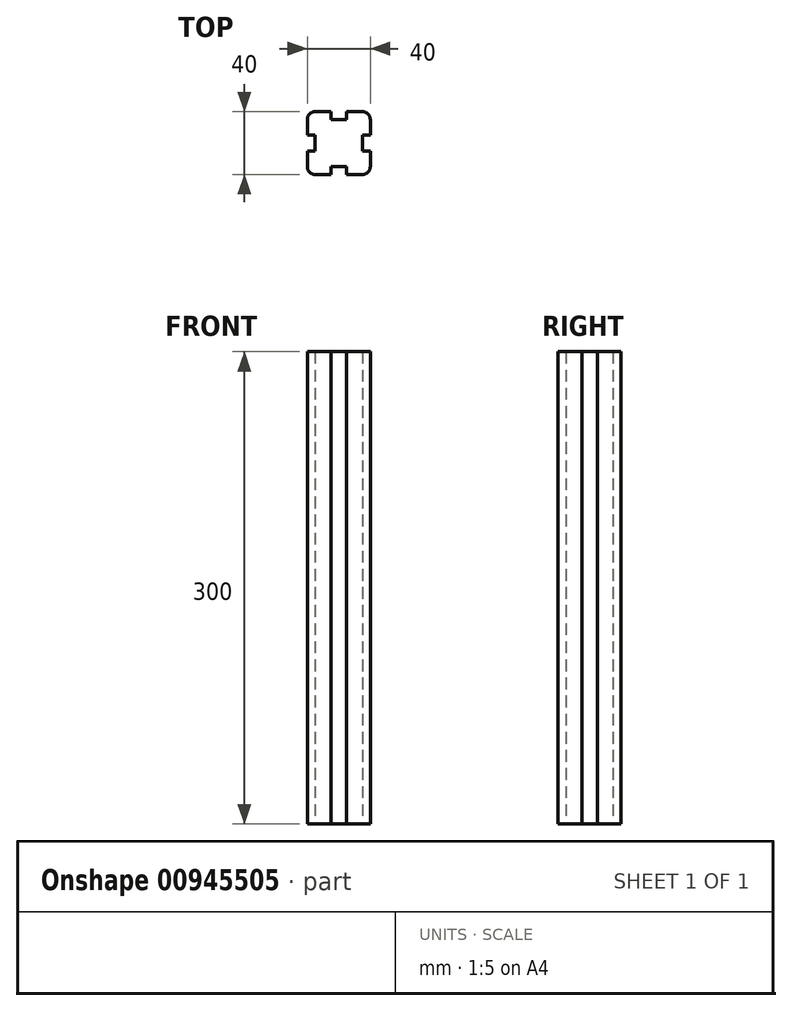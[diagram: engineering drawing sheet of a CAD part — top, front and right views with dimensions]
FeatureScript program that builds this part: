
annotation { "Feature Type Name" : "Feature", "Feature Type Description" : "" }
export const myFeature = defineFeature(function(context is Context, id is Id, definition is map)
    precondition{}
    {
        {
            var Q0;
            Q0=qCreatedBy(makeId("Top.planeOp"),FACE);
            var sketch = newSketch(context, id + "F0", { "sketchPlane" : qUnion([Q0])});
            skLineSegment(sketch, "E0.bottom", {"start": v(20, 20) * mm, "end": v(-20, 20) * mm});
            skLineSegment(sketch, "E0.top", {"start": v(20, -20) * mm, "end": v(-20, -20) * mm});
            skLineSegment(sketch, "E0.left", {"start": v(20, 20) * mm, "end": v(20, -20) * mm});
            skLineSegment(sketch, "E0.right", {"start": v(-20, 20) * mm, "end": v(-20, -20) * mm});
            skPoint(sketch, "E0.middle", {"position": v(0, 0) * mm});
            skLineSegment(sketch, "E1.bottom", {"start": v(-5, 20) * mm, "end": v(5, 20) * mm});
            skLineSegment(sketch, "E1.top", {"start": v(-5, 15) * mm, "end": v(5, 15) * mm});
            skLineSegment(sketch, "E1.left", {"start": v(-5, 20) * mm, "end": v(-5, 15) * mm});
            skLineSegment(sketch, "E1.right", {"start": v(5, 20) * mm, "end": v(5, 15) * mm});
            skLineSegment(sketch, "E2.bottom", {"start": v(-20, 5) * mm, "end": v(-15, 5) * mm});
            skLineSegment(sketch, "E2.top", {"start": v(-20, -5) * mm, "end": v(-15, -5) * mm});
            skLineSegment(sketch, "E2.left", {"start": v(-20, 5) * mm, "end": v(-20, -5) * mm});
            skLineSegment(sketch, "E2.right", {"start": v(-15, 5) * mm, "end": v(-15, -5) * mm});
            skLineSegment(sketch, "E3.MirrorCS", {"start": v(20, 5) * mm, "end": v(15, 5) * mm});
            skLineSegment(sketch, "E4.MirrorCS", {"start": v(15, 5) * mm, "end": v(15, -5) * mm});
            skLineSegment(sketch, "E5.MirrorCS", {"start": v(20, -5) * mm, "end": v(15, -5) * mm});
            skLineSegment(sketch, "E6.MirrorCS", {"start": v(-5, -20) * mm, "end": v(-5, -15) * mm});
            skLineSegment(sketch, "E7.MirrorCS", {"start": v(-5, -15) * mm, "end": v(5, -15) * mm});
            skLineSegment(sketch, "E8.MirrorCS", {"start": v(5, -20) * mm, "end": v(5, -15) * mm});
            skSolve(sketch);
        }
        {
            var Q0;
            Q0=makeQuery(id+"F0.imprint","IMPRINT",FACE,{"disambiguationData":[TD([[makeQuery(id+"F0.imprint","IMPRINT",EDGE,{"derivedFrom":sQuery(id+"F0.wireOp",EDGE,"E1.top")}),-1.0]])]});
            extrude(context, id + "F1", {"entities" : qUnion([Q0]), "endBound" : BoundingType.SYMMETRIC, "depth" : 300 * mm, "offsetDistance" : 25 * mm});
        }
        {
            var Q0;
            Q0=makeQuery(id+"F1.opExtrude","SWEPT_EDGE",EDGE,{"disambiguationData":[OSD([sQuery(id+"F0.wireOp",EDGE,"E0.bottom"),sQuery(id+"F0.wireOp",EDGE,"E0.left")])]});
            var Q1;
            Q1=makeQuery(id+"F1.opExtrude","SWEPT_EDGE",EDGE,{"disambiguationData":[OSD([sQuery(id+"F0.wireOp",EDGE,"E0.bottom"),sQuery(id+"F0.wireOp",EDGE,"E0.right")])]});
            var Q2;
            Q2=makeQuery(id+"F1.opExtrude","SWEPT_EDGE",EDGE,{"disambiguationData":[OSD([sQuery(id+"F0.wireOp",EDGE,"E0.top"),sQuery(id+"F0.wireOp",EDGE,"E0.right")])]});
            var Q3;
            Q3=makeQuery(id+"F1.opExtrude","SWEPT_EDGE",EDGE,{"disambiguationData":[OSD([sQuery(id+"F0.wireOp",EDGE,"E0.top"),sQuery(id+"F0.wireOp",EDGE,"E0.left")])]});
            fillet(context, id + "F2", {"entities" : qUnion([Q0, Q1, Q2, Q3]), "radius" : 5 * mm, "tangentPropagation" : true, "allowEdgeOverflow" : false});
        }
    });
